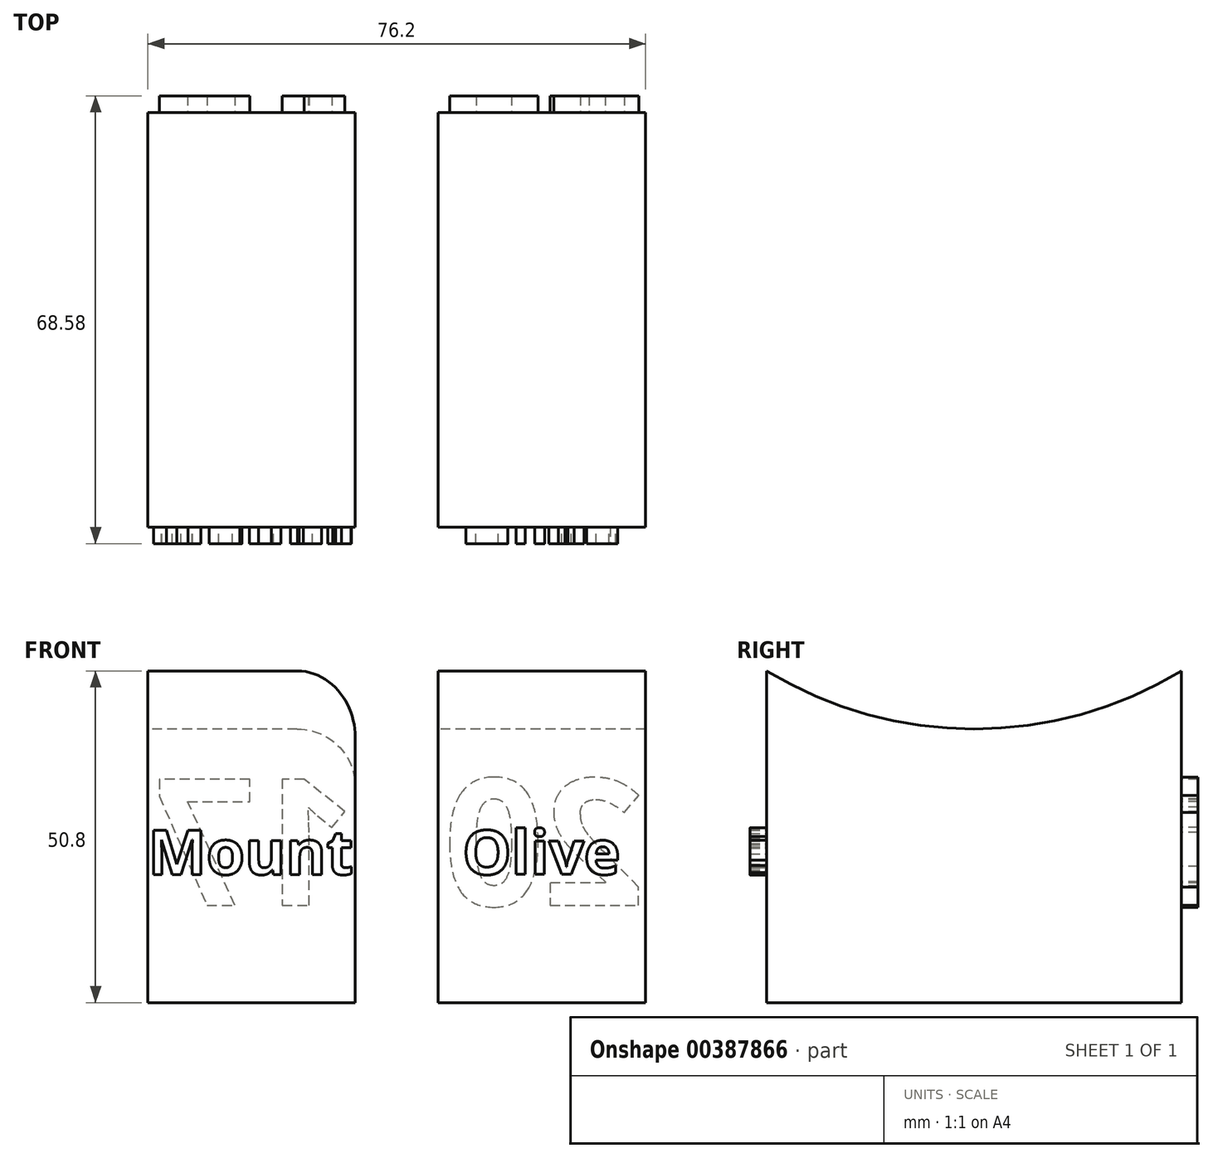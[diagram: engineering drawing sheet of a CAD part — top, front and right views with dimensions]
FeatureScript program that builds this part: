
annotation { "Feature Type Name" : "Feature", "Feature Type Description" : "" }
export const myFeature = defineFeature(function(context is Context, id is Id, definition is map)
    precondition{}
    {
        {
            var Q0;
            Q0=qCreatedBy(makeId("Top.planeOp"),FACE);
            var sketch = newSketch(context, id + "F0", { "sketchPlane" : qUnion([Q0])});
            skLineSegment(sketch, "E0.left", {"start": v(-44.45, 43.18) * mm, "end": v(-44.45, -33.02) * mm});
            skLineSegment(sketch, "E0.right", {"start": v(44.45, 43.18) * mm, "end": v(44.45, -33.02) * mm});
            skLineSegment(sketch, "E1", {"start": v(0, 0) * mm, "end": v(6.35, 0) * mm});
            skLineSegment(sketch, "E2", {"start": v(0, 0) * mm, "end": v(-6.35, 0) * mm});
            skLineSegment(sketch, "E3", {"start": v(-6.35, 0) * mm, "end": v(0, 0) * mm});
            skLineSegment(sketch, "E4", {"start": v(-44.45, 5.08) * mm, "end": v(-38.1, 5.08) * mm});
            skLineSegment(sketch, "E5", {"start": v(-44.45, 43.18) * mm, "end": v(0, 43.18) * mm});
            skLineSegment(sketch, "E6", {"start": v(44.45, 43.18) * mm, "end": v(0, 43.18) * mm});
            skLineSegment(sketch, "E7", {"start": v(-44.45, -33.02) * mm, "end": v(0, -33.02) * mm});
            skLineSegment(sketch, "E8", {"start": v(0, -33.02) * mm, "end": v(44.45, -33.02) * mm});
            skLineSegment(sketch, "E9", {"start": v(22.23, -33.02) * mm, "end": v(22.23, -26.67) * mm});
            skPoint(sketch, "E9.endSnap0", {"position": v(22.23, -33.02) * mm});
            skLineSegment(sketch, "E10", {"start": v(-22.23, -33.02) * mm, "end": v(-22.23, -26.67) * mm});
            skPoint(sketch, "E10.endSnap0", {"position": v(-22.23, -33.02) * mm});
            skPoint(sketch, "E11", {"position": v(-38.1, 36.83) * mm});
            skPoint(sketch, "E12", {"position": v(-38.1, -26.67) * mm});
            skPoint(sketch, "E13", {"position": v(38.1, -26.67) * mm});
            skPoint(sketch, "E14", {"position": v(38.1, 36.83) * mm});
            skLineSegment(sketch, "E15", {"start": v(-22.23, -26.67) * mm, "end": v(22.23, -26.67) * mm, "construction": true});
            skPoint(sketch, "E16", {"position": v(-6.35, -26.67) * mm});
            skPoint(sketch, "E17", {"position": v(6.35, -26.67) * mm});
            skLineSegment(sketch, "E18.bottom", {"start": v(-38.1, 36.83) * mm, "end": v(-6.35, 36.83) * mm});
            skLineSegment(sketch, "E18.top", {"start": v(-38.1, -26.67) * mm, "end": v(-6.35, -26.67) * mm});
            skLineSegment(sketch, "E18.left", {"start": v(-38.1, 36.83) * mm, "end": v(-38.1, -26.67) * mm});
            skLineSegment(sketch, "E18.right", {"start": v(-6.35, 36.83) * mm, "end": v(-6.35, -26.67) * mm});
            skLineSegment(sketch, "E19.bottom", {"start": v(6.35, -26.67) * mm, "end": v(38.1, -26.67) * mm});
            skLineSegment(sketch, "E19.top", {"start": v(6.35, 36.83) * mm, "end": v(38.1, 36.83) * mm});
            skLineSegment(sketch, "E19.left", {"start": v(6.35, -26.67) * mm, "end": v(6.35, 36.83) * mm});
            skLineSegment(sketch, "E19.right", {"start": v(38.1, -26.67) * mm, "end": v(38.1, 36.83) * mm});
            skLineSegment(sketch, "E20", {"start": v(0, 43.18) * mm, "end": v(0, -33.02) * mm});
            skLineSegment(sketch, "E21", {"start": v(44.45, 0) * mm, "end": v(38.1, 0) * mm});
            skLineSegment(sketch, "E22", {"start": v(-22.23, 43.18) * mm, "end": v(-22.23, 36.83) * mm});
            skLineSegment(sketch, "E23", {"start": v(22.23, 43.18) * mm, "end": v(22.22, 36.83) * mm});
            skSolve(sketch);
        }
        {
            var Q0;
            {var subQ4=sQuery(id+"F0.wireOp",EDGE,"E18.left");var subQ6=sQuery(id+"F0.wireOp",EDGE,"E18.bottom");var subQ9=makeQuery(id+"F0.imprint","INTERSECT",VERTEX,{"derivedFrom":[subQ6,subQ4]});Q0=makeQuery(id+"F0.imprint","IMPRINT",FACE,{"disambiguationData":[TD([[makeQuery(id+"F0.imprint","IMPRINT",EDGE,{"disambiguationData":[TD([[subQ9,-1.0]])],"derivedFrom":subQ6}),-1.0]])]});}
            var Q1;
            {var subQ6=sQuery(id+"F0.wireOp",EDGE,"E19.bottom");var subQ7=makeQuery(id+"F0.imprint","INTERSECT",VERTEX,{"derivedFrom":[sQuery(id+"F0.wireOp",EDGE,"E9"),subQ6]});Q1=makeQuery(id+"F0.imprint","IMPRINT",FACE,{"disambiguationData":[TD([[makeQuery(id+"F0.imprint","IMPRINT",EDGE,{"disambiguationData":[TD([[subQ7,1.0]])],"derivedFrom":subQ6}),1.0]])]});}
            extrude(context, id + "F1", {"entities" : qUnion([Q0, Q1]), "depth" : 50.8 * mm});
        }
        {
            var Q0;
            Q0=makeQuery(id+"F1.opExtrude","SWEPT_FACE",FACE,{"disambiguationData":[OSD([sQuery(id+"F0.wireOp",EDGE,"E19.right")])]});
            var sketch = newSketch(context, id + "F2", { "sketchPlane" : qUnion([Q0])});
            skArc(sketch, "E24", {"start": v(-26.67, 50.8) * mm, "mid": v(5.08, 41.91) * mm, "end": v(36.83, 50.8) * mm});
            skSolve(sketch);
        }
        {
            var Q0;
            Q0=makeQuery(id+"F1.opExtrude","SWEPT_FACE",FACE,{"disambiguationData":[OSD([sQuery(id+"F0.wireOp",EDGE,"E18.left")])]});
            var sketch = newSketch(context, id + "F3", { "sketchPlane" : qUnion([Q0])});
            skArc(sketch, "E25", {"start": v(-36.83, 50.8) * mm, "mid": v(-5.08, 41.91) * mm, "end": v(26.67, 50.8) * mm});
            skSolve(sketch);
        }
        {
            var Q0;
            Q0=makeQuery(id+"F3.imprint","IMPRINT",FACE,{"disambiguationData":[TD([[makeQuery(id+"F3.imprint","IMPRINT",EDGE,{"derivedFrom":sQuery(id+"F3.wireOp",EDGE,"E25")}),1.0]])]});
            extrude(context, id + "F4", {"entities" : qUnion([Q0]), "operationType" : NewBodyOperationType.REMOVE, "oppositeDirection" : true, "depth" : 76.2 * mm});
        }
        {
            var Q0;
            Q0=makeQuery(id+"F2.imprint","IMPRINT",FACE,{"disambiguationData":[TD([[makeQuery(id+"F2.imprint","IMPRINT",EDGE,{"derivedFrom":sQuery(id+"F2.wireOp",EDGE,"E24")}),1.0]])]});
            extrude(context, id + "F5", {"entities" : qUnion([Q0]), "operationType" : NewBodyOperationType.REMOVE, "oppositeDirection" : true, "depth" : 76.2 * mm});
        }
        {
            var Q0;
            Q0=makeQuery(id+"F5.boolean.opBoolean","COPY",EDGE,{"derivedFrom":makeQuery(id+"F5.opExtrude","CAP_EDGE",EDGE,{"disambiguationData":[OSD([sQuery(id+"F2.wireOp",EDGE,"E24")])],"isStart":true})});
            var Q1;
            Q1=makeQuery(id+"F5.boolean.opBoolean","INTERSECT",EDGE,{"derivedFrom":[makeQuery(id+"F1.opExtrude","SWEPT_FACE",FACE,{"disambiguationData":[OSD([sQuery(id+"F0.wireOp",EDGE,"E19.left")])]}),makeQuery(id+"F5.opExtrude","SWEPT_FACE",FACE,{"disambiguationData":[OSD([sQuery(id+"F2.wireOp",EDGE,"E24")])]})]});
            var Q2;
            Q2=makeQuery(id+"F4.boolean.opBoolean","COPY",EDGE,{"derivedFrom":makeQuery(id+"F4.opExtrude","CAP_EDGE",EDGE,{"disambiguationData":[OSD([sQuery(id+"F3.wireOp",EDGE,"E25")])],"isStart":true})});
            var Q3;
            Q3=makeQuery(id+"F4.boolean.opBoolean","INTERSECT",EDGE,{"derivedFrom":[makeQuery(id+"F1.opExtrude","SWEPT_FACE",FACE,{"disambiguationData":[OSD([sQuery(id+"F0.wireOp",EDGE,"E18.right")])]}),makeQuery(id+"F4.opExtrude","SWEPT_FACE",FACE,{"disambiguationData":[OSD([sQuery(id+"F3.wireOp",EDGE,"E25")])]})]});
            fillet(context, id + "F6", {"entities" : qUnion([Q0, Q1, Q2, Q3]), "radius" : 8.9 * mm, "tangentPropagation" : true, "allowEdgeOverflow" : false});
        }
        {
            var Q0;
            Q0=makeQuery(id+"F1.opExtrude","SWEPT_FACE",FACE,{"disambiguationData":[OSD([sQuery(id+"F0.wireOp",EDGE,"E18.top")])]});
            var sketch = newSketch(context, id + "F7", { "sketchPlane" : qUnion([Q0])});
            skText(sketch, "E26", { "text": "Mount", "fontName": "OpenSans-Bold.ttf"});
            skLineSegment(sketch, "E27", {"start": v(-6.35, 26.46) * mm, "end": v(47.52, 26.46) * mm});
            skLineSegment(sketch, "E28", {"start": v(-6.35, 19.62) * mm, "end": v(47.52, 19.62) * mm});
            const initialGuessF7  = {"E26": [-0.0381, 0.01962, 1, 0, 0.00684]};
            skSetInitialGuess(sketch, initialGuessF7);
            skSolve(sketch);
        }
        {
            var Q0;
            Q0=makeQuery(id+"F1.opExtrude","SWEPT_FACE",FACE,{"disambiguationData":[OSD([sQuery(id+"F0.wireOp",EDGE,"E19.bottom")])]});
            var sketch = newSketch(context, id + "F8", { "sketchPlane" : qUnion([Q0])});
            skText(sketch, "E29", { "text": "Olive", "fontName": "OpenSans-Bold.ttf"});
            const initialGuessF8  = {"E29": [0.01006, 0.01963, 1, 0, 0.00678]};
            skSetInitialGuess(sketch, initialGuessF8);
            skSolve(sketch);
        }
        {
            var Q0;
            Q0 = qSketchRegion(id + "F8", true);
            var Q1;
            Q1 = qSketchRegion(id + "F7", true);
            extrude(context, id + "F9", {"entities" : qUnion([Q0, Q1]), "depth" : 2.54 * mm});
        }
        {
            var Q0;
            Q0=makeQuery(id+"F1.opExtrude","SWEPT_FACE",FACE,{"disambiguationData":[OSD([sQuery(id+"F0.wireOp",EDGE,"E19.top")])]});
            var sketch = newSketch(context, id + "F10", { "sketchPlane" : qUnion([Q0])});
            skText(sketch, "E30", { "text": "20", "fontName": "OpenSans-Bold.ttf"});
            skLineSegment(sketch, "E31", {"start": v(-6.35, 34.4) * mm, "end": v(46.53, 34.4) * mm});
            skLineSegment(sketch, "E32", {"start": v(-6.35, 14.87) * mm, "end": v(46.53, 14.87) * mm});
            const initialGuessF10  = {"E30": [-0.0381, 0.01487, 1, 0, 0.01953]};
            skSetInitialGuess(sketch, initialGuessF10);
            skSolve(sketch);
        }
        {
            var Q0;
            Q0=makeQuery(id+"F1.opExtrude","SWEPT_FACE",FACE,{"disambiguationData":[OSD([sQuery(id+"F0.wireOp",EDGE,"E18.bottom")])]});
            var sketch = newSketch(context, id + "F11", { "sketchPlane" : qUnion([Q0])});
            skText(sketch, "E33", { "text": "17", "fontName": "OpenSans-Bold.ttf"});
            const initialGuessF11  = {"E33": [0.00635, 0.01492, 1, 0, 0.01946]};
            skSetInitialGuess(sketch, initialGuessF11);
            skSolve(sketch);
        }
        {
            var Q0;
            Q0=makeQuery(id+"F10.imprint","IMPRINT",FACE,{"disambiguationData":[TD([[makeQuery(id+"F10.imprint","IMPRINT",EDGE,{"derivedFrom":sQuery(id+"F10.wireOp",EDGE,"E30.sketch_text.stroke-24")}),-1.0]])]});
            var Q1;
            Q1=makeQuery(id+"F10.imprint","IMPRINT",FACE,{"disambiguationData":[TD([[makeQuery(id+"F10.imprint","IMPRINT",EDGE,{"derivedFrom":sQuery(id+"F10.wireOp",EDGE,"E30.sketch_text.stroke-0")}),-1.0]])]});
            var Q2;
            Q2=makeQuery(id+"F11.imprint","IMPRINT",FACE,{"disambiguationData":[TD([[makeQuery(id+"F11.imprint","IMPRINT",EDGE,{"derivedFrom":sQuery(id+"F11.wireOp",EDGE,"E33.sketch_text.stroke-0")}),-1.0]])]});
            var Q3;
            Q3=makeQuery(id+"F11.imprint","IMPRINT",FACE,{"disambiguationData":[TD([[makeQuery(id+"F11.imprint","IMPRINT",EDGE,{"derivedFrom":sQuery(id+"F11.wireOp",EDGE,"E33.sketch_text.stroke-10")}),-1.0]])]});
            extrude(context, id + "F12", {"entities" : qUnion([Q0, Q1, Q2, Q3]), "depth" : 2.54 * mm});
        }
    });
